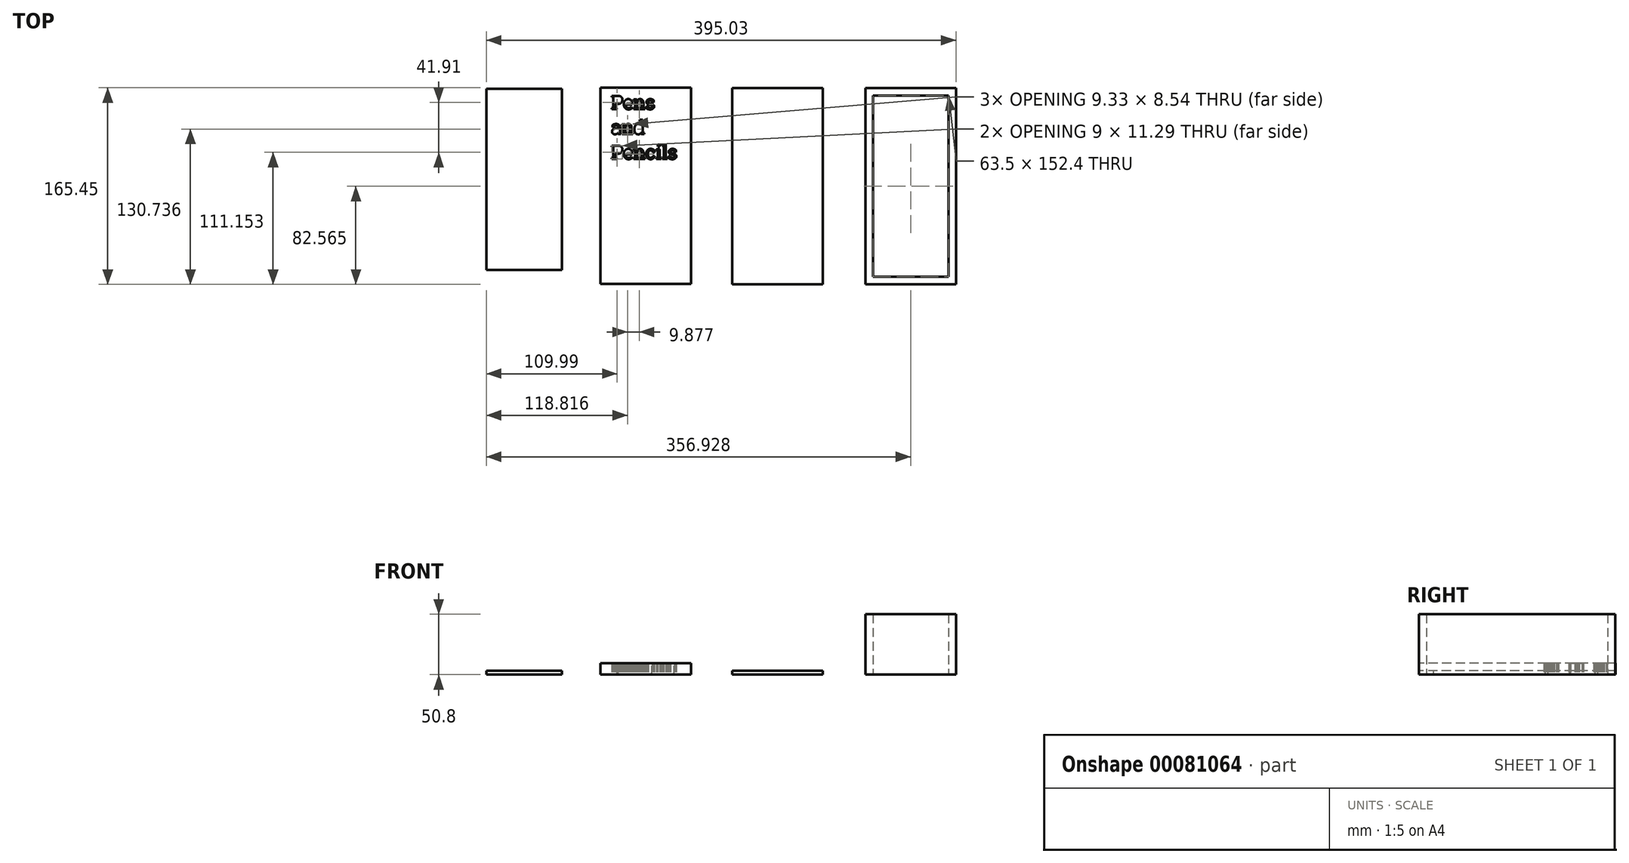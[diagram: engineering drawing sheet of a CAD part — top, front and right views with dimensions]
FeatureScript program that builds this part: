
annotation { "Feature Type Name" : "Feature", "Feature Type Description" : "" }
export const myFeature = defineFeature(function(context is Context, id is Id, definition is map)
    precondition{}
    {
        {
            var Q0;
            Q0=qCreatedBy(makeId("Top.planeOp"),FACE);
            var sketch = newSketch(context, id + "F0", { "sketchPlane" : qUnion([Q0])});
            skLineSegment(sketch, "E0.bottom", {"start": v(47.34, 90.3) * mm, "end": v(123.54, 90.3) * mm});
            skLineSegment(sketch, "E0.top", {"start": v(47.34, -74.8) * mm, "end": v(123.54, -74.8) * mm});
            skLineSegment(sketch, "E0.left", {"start": v(47.34, 90.3) * mm, "end": v(47.34, -74.8) * mm});
            skLineSegment(sketch, "E0.right", {"start": v(123.54, 90.3) * mm, "end": v(123.54, -74.8) * mm});
            skLineSegment(sketch, "E1.bottom", {"start": v(-64.6, 90.28) * mm, "end": v(11.6, 90.28) * mm});
            skLineSegment(sketch, "E1.top", {"start": v(-64.6, -74.82) * mm, "end": v(11.6, -74.82) * mm});
            skLineSegment(sketch, "E1.left", {"start": v(-64.6, 90.28) * mm, "end": v(-64.6, -74.82) * mm});
            skLineSegment(sketch, "E1.right", {"start": v(11.6, 90.28) * mm, "end": v(11.6, -74.82) * mm});
            skLineSegment(sketch, "E2.bottom", {"start": v(-175.44, 90.63) * mm, "end": v(-99.24, 90.63) * mm});
            skLineSegment(sketch, "E2.top", {"start": v(-175.44, -74.47) * mm, "end": v(-99.24, -74.47) * mm});
            skLineSegment(sketch, "E2.left", {"start": v(-175.44, 90.63) * mm, "end": v(-175.44, -74.47) * mm});
            skLineSegment(sketch, "E2.right", {"start": v(-99.24, 90.63) * mm, "end": v(-99.24, -74.47) * mm});
            skLineSegment(sketch, "E3.bottom", {"start": v(-271.49, 89.93) * mm, "end": v(-207.99, 89.93) * mm});
            skLineSegment(sketch, "E3.top", {"start": v(-271.49, -62.47) * mm, "end": v(-207.99, -62.47) * mm});
            skLineSegment(sketch, "E3.left", {"start": v(-271.49, 89.93) * mm, "end": v(-271.49, -62.47) * mm});
            skLineSegment(sketch, "E3.right", {"start": v(-207.99, 89.93) * mm, "end": v(-207.99, -62.47) * mm});
            skLineSegment(sketch, "E4.bottom", {"start": v(53.69, 83.95) * mm, "end": v(117.19, 83.95) * mm});
            skLineSegment(sketch, "E4.top", {"start": v(53.69, -68.45) * mm, "end": v(117.19, -68.45) * mm});
            skLineSegment(sketch, "E4.left", {"start": v(53.69, 83.95) * mm, "end": v(53.69, -68.45) * mm});
            skLineSegment(sketch, "E4.right", {"start": v(117.19, 83.95) * mm, "end": v(117.19, -68.45) * mm});
            skText(sketch, "E5", { "text": "Pens\nand\nPencils", "fontName": "RobotoSlab-Regular.ttf"});
            const initialGuessF0  = {"E5": [-0.16655, 0.0726, 1, 0, 0.01143]};
            skSetInitialGuess(sketch, initialGuessF0);
            skSolve(sketch);
        }
        {
            var Q0;
            Q0=makeQuery(id+"F0.imprint","IMPRINT",FACE,{"disambiguationData":[TD([[makeQuery(id+"F0.imprint","IMPRINT",EDGE,{"derivedFrom":sQuery(id+"F0.wireOp",EDGE,"E2.bottom")}),-1.0]])]});
            extrude(context, id + "F1", {"entities" : qUnion([Q0]), "depth" : 9.52 * mm});
        }
        {
            var Q0;
            Q0=makeQuery(id+"F0.imprint","IMPRINT",FACE,{"disambiguationData":[TD([[makeQuery(id+"F0.imprint","IMPRINT",EDGE,{"derivedFrom":sQuery(id+"F0.wireOp",EDGE,"E3.bottom")}),-1.0]])]});
            var Q1;
            Q1=makeQuery(id+"F0.imprint","IMPRINT",FACE,{"disambiguationData":[TD([[makeQuery(id+"F0.imprint","IMPRINT",EDGE,{"derivedFrom":sQuery(id+"F0.wireOp",EDGE,"E1.bottom")}),-1.0]])]});
            extrude(context, id + "F2", {"entities" : qUnion([Q0, Q1]), "depth" : 3.17 * mm});
        }
        {
            var Q0;
            Q0=makeQuery(id+"F0.imprint","IMPRINT",FACE,{"disambiguationData":[TD([[makeQuery(id+"F0.imprint","IMPRINT",EDGE,{"derivedFrom":sQuery(id+"F0.wireOp",EDGE,"E0.bottom")}),-1.0]])]});
            extrude(context, id + "F3", {"entities" : qUnion([Q0]), "depth" : 50.8 * mm});
        }
    });
